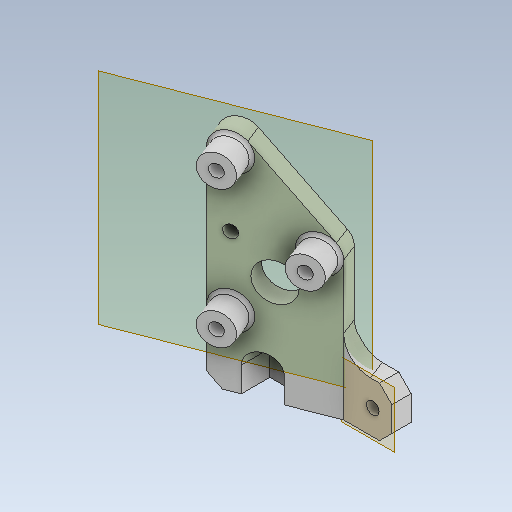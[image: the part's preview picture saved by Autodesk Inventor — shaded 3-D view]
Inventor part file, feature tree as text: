
AUTODESK INVENTOR PART (.ipt)
format: ipt  version: 2020 (Build 240168000, 168)  size: 313,856 bytes
history: native  units: mm
features: extrude x10, sketch x10, reference x10, other x8, projected_geometry x5, plane x3, fillet x3, thicken_offset x1, chamfer x1
ambient origin geometry x8: Origin, YZ Plane, XZ Plane, XY Plane, X Axis, Y Axis, Z Axis, Center Point
bodies: Solid1 (feature_tree)
feature tree (51):
  plane  "Work Plane1"
  extrude  "Extrusion1"  Depth=6.0mm
  sketch  "Sketch4"  dims[d6=6.0mm d7=3.0mm]
  plane  "Work Plane2"
  extrude  "Extrusion2"  Depth=3.0mm
  extrude  "Extrusion3"  Depth=3.0mm
  extrude  "Extrusion4"  Depth=3.0mm TaperAngle=0.0deg
  extrude  "Extrusion5"  Depth=10.0mm
  plane  "Work Plane3"
  extrude  "Extrusion6"  Depth=10.0mm TaperAngle=0.0deg
  extrude  "Extrusion7"  Depth=7.0mm
  thicken_offset  "Thicken1"
  fillet  "Fillet1"  Radius=5.0mm
  chamfer  "Chamfer2"  Distance=10.0mm
  fillet  "Fillet2"  Radius=2.0mm
  extrude  "Extrusion8"  Depth=2.0mm
  extrude  "Extrusion9"  Depth=10.0mm
  extrude  "Extrusion10"  Depth=4.0mm
  fillet  "Fillet3"  Radius=2.0mm
  sketch  "Sketch2"  dims[d4=6.0mm d5=6.0mm]
  reference  "Reference4"
  reference  "Reference5"
  reference  "Reference6"
  reference  "Reference9"
  projected_geometry  "Projected Loop2"
  sketch  "Sketch5"  dims[d8=3.0mm d9=0.0mm d11=3.0mm]
  projected_geometry  "Projected Loop3"
  sketch  "Sketch6"  dims[d12=3.0mm d13=0.0mm d14=3.0mm d15=0.0mm]
  projected_geometry  "Projected Loop4"
  sketch  "Sketch7"  dims[d19=10.0mm d20=0.0mm d21=2.0mm]
  reference  "Reference10"
  reference  "Reference11"
  sketch  "Sketch8"  dims[d22=2.0mm d23=10.0mm d24=0.0mm]
  sketch  "Sketch9"  dims[d25=0.0mm d26=7.0mm d27=5.0mm d28=10.0mm d29=0.0mm d30=2.0mm]
  reference  "Reference12"
  reference  "Reference13"
  reference  "Reference14"
  sketch  "Sketch10"  dims[d31=2.0mm d32=2.0mm]
  reference  "Reference15"
  sketch  "Sketch11"  dims[d33=10.0mm d34=0.0mm d35=0.2mm]
  projected_geometry  "Projected Loop5"
  sketch  "Sketch12"  dims[d36=0.2mm d37=4.0mm d38=2.0mm d39=2.0mm d40=45.0deg d41=1.0mm d45=2.0mm d46=10.0mm d47=0.0mm d48=6.0mm d49=10.0mm d50=0.0mm d51=5.0mm d52=5.0mm d53=5.0mm d54=4.0mm d55=0.0mm d56=0.5mm d57=0.872665mm]
  projected_geometry  "Projected Loop6"
  parser-record x1  (decoder bookkeeping rows leaked as tree rows — omitted from the tree; the rows remain in map.json)
  other  "leg_1.iam"
  other  "wh_ass_3:3"
  other  "screw_holder_2_3:2"
  other  "screw_holder_2_3:5"
  other  "screw_holder_2_3:1"
  other  "leg_holder_2:1"
  other  "tendon_wh_3:1"
note: 1 file-system path scrubbed to <path> (originals preserved in map.json)
